# Revit family: Table-Teknion-CQTHR_Rectangular_High_Table-R2020
name_source: partatom
category: Furniture
units: mm (PartAtom-declared; Revit-internal decimal feet)

## family parameters
Always vertical = Yes
Cut with Voids When Loaded = No
OmniClass Number = 23.40.20.00
OmniClass Title = General Furniture and Specialties
Room Calculation Point = No
Shared = Yes
Work Plane-Based = No

## types (8) — shared parameters
Assembly Code = E2020200
Manufacturer = Teknion
Manufacturer Fax = 416.661.4586
Part Number = CQTHR
Product Documentation Link = https://assets.teknion.com
Product Line = Routes Tables
Product Page URL = https://www.teknion.com
Series = Routes
Sustainability Data = https://www.teknion.com
URL = www.teknion.com
Unit Weight URL = http://www.teknion.com
Warranty = http://www.teknion.com
zero-valued in all types: Default Elevation

## per-type parameters (varying)
| type | Caster | Description | Fixed Legs W(60) | Fixed legs W(72) | Height | Mobile Legs W(60) | Mobile Legs W(72) | Model | Width |
| Bar Height Fixed Mobility W60 | No | Rectangular Height Table Bar Height Fixed Mobility 30Dx60W | Yes | No | 42 " | No | No | CQTHRBF3060 | 60 " |
| Bar Height Mobile Mobility W60 | Yes | Rectangular Height Table Bar Height Mobile Mobility 30Dx60W | No | No | 42 " | Yes | No | CQTHRBM3060 | 60 " |
| Counter Height Fixed Mobility W72 | No | Rectangular Height Table Counter Height Fixed Mobility 30Dx72W | No | Yes | 36 " | No | No | CQTHRCF3072 | 72 " |
| Counter Height Mobile Mobility W72 | Yes | Rectangular Height Table Counter Height Mobile Mobility 30Dx72W | No | No | 36 " | No | Yes | CQTHRCM3072 | 72 " |
| Bar Height Fixed Mobility W72 | No | Rectangular Height Table Bar Height Fixed Mobility 30Dx72W | No | Yes | 42 " | No | No | CQTHRBF3072 | 72 " |
| Bar Height Mobile Mobility W72 | Yes | Rectangular Height Table Bar Height Mobile Mobility 30Dx72W | No | No | 42 " | No | Yes | CQTHRBM3072 | 72 " |
| Counter Height Fixed Mobility W60 | No | Rectangular Height Table Counter Height Fixed Mobility 30Dx60W | Yes | No | 36 " | No | No | CQTHRCF3060 | 60 " |
| Counter Height Mobile Mobility W60 | Yes | Rectangular Height Table Counter Height Mobile Mobility 30Dx60W | No | No | 36 " | Yes | No | CQTHRCM3060 | 60 " |

## geometry (parser evidence)
native form markers: Sweep x3
no freeform markers — native parametric forms only
